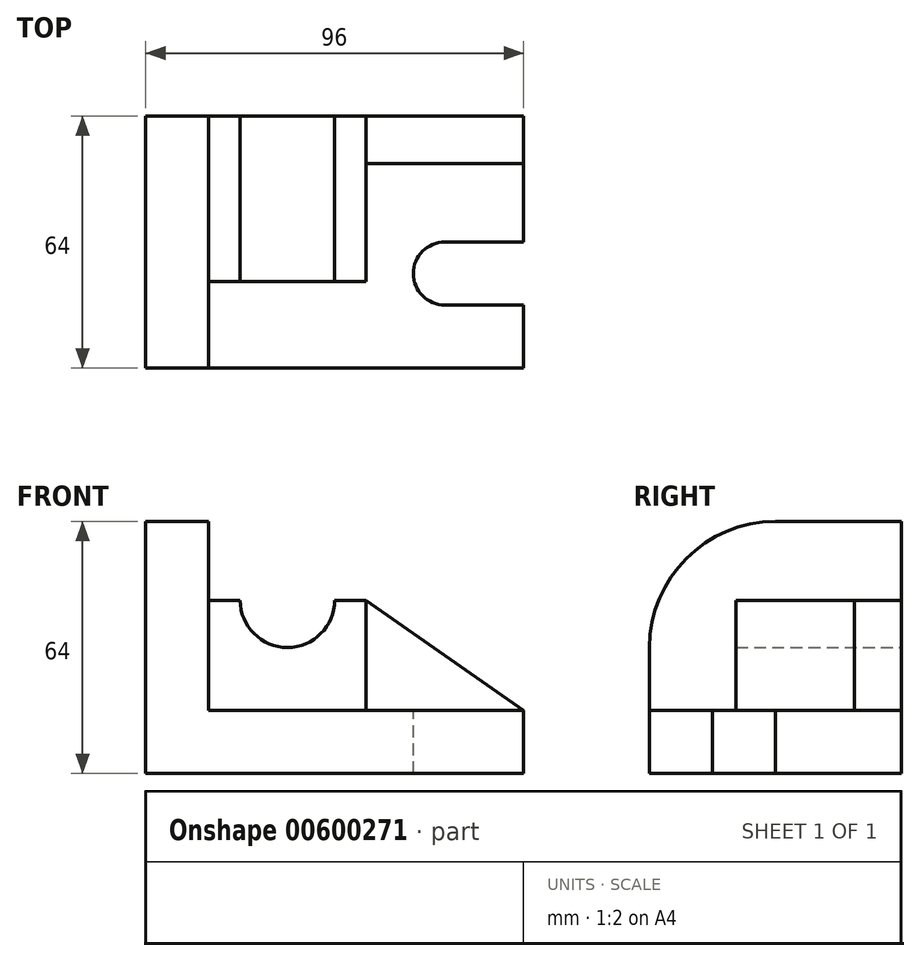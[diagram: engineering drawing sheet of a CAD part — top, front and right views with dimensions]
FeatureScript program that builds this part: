
annotation { "Feature Type Name" : "Feature", "Feature Type Description" : "" }
export const myFeature = defineFeature(function(context is Context, id is Id, definition is map)
    precondition{}
    {
        {
            var Q0;
            Q0=qCreatedBy(makeId("Top.planeOp"),FACE);
            var sketch = newSketch(context, id + "F0", { "sketchPlane" : qUnion([Q0])});
            skLineSegment(sketch, "E0.bottom", {"start": v(-48.61, -37.44) * mm, "end": v(47.39, -37.44) * mm});
            skLineSegment(sketch, "E0.top", {"start": v(-48.61, 26.56) * mm, "end": v(47.39, 26.56) * mm});
            skLineSegment(sketch, "E0.left", {"start": v(-48.61, -37.44) * mm, "end": v(-48.61, 26.56) * mm});
            skLineSegment(sketch, "E0.right", {"start": v(47.39, -37.44) * mm, "end": v(47.39, 26.56) * mm});
            skSolve(sketch);
        }
        {
            var Q0;
            Q0 = qSketchRegion(id + "F0", true);
            extrude(context, id + "F1", {"entities" : qUnion([Q0]), "depth" : 16 * mm, "offsetDistance" : 25 * mm});
        }
        {
            var Q0;
            Q0=makeQuery(id+"F1.opExtrude","SWEPT_FACE",FACE,{"disambiguationData":[OSD([sQuery(id+"F0.wireOp",EDGE,"E0.left")])]});
            var sketch = newSketch(context, id + "F2", { "sketchPlane" : qUnion([Q0])});
            skLineSegment(sketch, "E1", {"start": v(-26.56, 16) * mm, "end": v(-26.56, 64) * mm});
            skLineSegment(sketch, "E2", {"start": v(-26.56, 64) * mm, "end": v(5.44, 64) * mm});
            skLineSegment(sketch, "E3", {"start": v(-26.56, 16) * mm, "end": v(37.44, 16) * mm});
            skLineSegment(sketch, "E4", {"start": v(37.44, 16) * mm, "end": v(37.44, 32) * mm});
            skArc(sketch, "E5", {"start": v(5.44, 64) * mm, "mid": v(28.06, 54.63) * mm, "end": v(37.44, 32) * mm});
            skSolve(sketch);
        }
        {
            var Q0;
            Q0 = qSketchRegion(id + "F2", true);
            extrude(context, id + "F3", {"entities" : qUnion([Q0]), "operationType" : NewBodyOperationType.ADD, "oppositeDirection" : true, "depth" : 16 * mm, "offsetDistance" : 25 * mm});
        }
        {
            var Q0;
            Q0=makeQuery(id+"F3.boolean.opBoolean","MERGE",FACE,{"derivedFrom":[makeQuery(id+"F1.opExtrude","SWEPT_FACE",FACE,{"disambiguationData":[OSD([sQuery(id+"F0.wireOp",EDGE,"E0.top")])]}),makeQuery(id+"F3.opExtrude","SWEPT_FACE",FACE,{"disambiguationData":[OSD([sQuery(id+"F2.wireOp",EDGE,"E1")])]})]});
            var sketch = newSketch(context, id + "F4", { "sketchPlane" : qUnion([Q0])});
            skLineSegment(sketch, "E6", {"start": v(32.61, 16) * mm, "end": v(-7.39, 16) * mm});
            skLineSegment(sketch, "E7", {"start": v(-7.39, 16) * mm, "end": v(-7.39, 44) * mm});
            skLineSegment(sketch, "E8", {"start": v(-7.39, 44) * mm, "end": v(32.61, 44) * mm});
            skSolve(sketch);
        }
        {
            var Q0;
            {var subQ0=sQuery(id+"F4.wireOp",EDGE,"E6");Q0=makeQuery(id+"F4.imprint","IMPRINT",FACE,{"disambiguationData":[TD([[makeQuery(id+"F4.imprint","IMPRINT",EDGE,{"derivedFrom":subQ0}),-1.0]])]});}
            extrude(context, id + "F5", {"entities" : qUnion([Q0]), "operationType" : NewBodyOperationType.ADD, "oppositeDirection" : true, "depth" : 42 * mm, "offsetDistance" : 25 * mm});
        }
        {
            var Q0;
            {var subQ0=sQuery(id+"F2.wireOp",EDGE,"E1");Q0=makeQuery(id+"F5.boolean.opBoolean","MERGE",FACE,{"derivedFrom":[makeQuery(id+"F3.boolean.opBoolean","MERGE",FACE,{"derivedFrom":[makeQuery(id+"F1.opExtrude","SWEPT_FACE",FACE,{"disambiguationData":[OSD([sQuery(id+"F0.wireOp",EDGE,"E0.top")])]}),makeQuery(id+"F3.opExtrude","SWEPT_FACE",FACE,{"disambiguationData":[OSD([subQ0])]})]}),makeQuery(id+"F5.opExtrude","CAP_FACE",FACE,{"disambiguationData":[OSD([subQ0,sQuery(id+"F4.wireOp",EDGE,"E6"),sQuery(id+"F4.wireOp",EDGE,"E7"),sQuery(id+"F4.wireOp",EDGE,"E8")])],"isStart":true})]});}
            var sketch = newSketch(context, id + "F6", { "sketchPlane" : qUnion([Q0])});
            skArc(sketch, "E9", {"start": v(0.61, 44) * mm, "mid": v(12.61, 32) * mm, "end": v(24.61, 44) * mm});
            skLineSegment(sketch, "E10", {"start": v(0.61, 44) * mm, "end": v(24.61, 44) * mm});
            skSolve(sketch);
        }
        {
            var Q0;
            Q0 = qSketchRegion(id + "F6", true);
            extrude(context, id + "F7", {"entities" : qUnion([Q0]), "operationType" : NewBodyOperationType.REMOVE, "oppositeDirection" : true, "depth" : 42 * mm, "offsetDistance" : 25 * mm});
        }
        {
            var Q0;
            Q0=makeQuery(id+"F1.opExtrude","CAP_FACE",FACE,{"disambiguationData":[OSD([sQuery(id+"F0.wireOp",EDGE,"E0.bottom"),sQuery(id+"F0.wireOp",EDGE,"E0.top"),sQuery(id+"F0.wireOp",EDGE,"E0.left"),sQuery(id+"F0.wireOp",EDGE,"E0.right")])],"isStart":false});
            var sketch = newSketch(context, id + "F8", { "sketchPlane" : qUnion([Q0])});
            skLineSegment(sketch, "E11.bottom", {"start": v(47.39, -21.44) * mm, "end": v(27.39, -21.44) * mm});
            skLineSegment(sketch, "E11.top", {"start": v(47.39, -5.44) * mm, "end": v(27.39, -5.44) * mm});
            skLineSegment(sketch, "E11.left", {"start": v(47.39, -21.44) * mm, "end": v(47.39, -5.44) * mm});
            skLineSegment(sketch, "E11.right", {"start": v(27.39, -21.44) * mm, "end": v(27.39, -5.44) * mm});
            skArc(sketch, "E12", {"start": v(27.39, -21.44) * mm, "mid": v(19.39, -13.44) * mm, "end": v(27.39, -5.44) * mm});
            skSolve(sketch);
        }
        {
            var Q0;
            Q0=makeQuery(id+"F8.imprint","IMPRINT",FACE,{"disambiguationData":[TD([[makeQuery(id+"F8.imprint","IMPRINT",EDGE,{"derivedFrom":sQuery(id+"F8.wireOp",EDGE,"E11.right")}),1.0]])]});
            var Q1;
            Q1=makeQuery(id+"F8.imprint","IMPRINT",FACE,{"disambiguationData":[TD([[makeQuery(id+"F8.imprint","IMPRINT",EDGE,{"derivedFrom":sQuery(id+"F8.wireOp",EDGE,"E11.bottom")}),-1.0]])]});
            extrude(context, id + "F9", {"entities" : qUnion([Q0, Q1]), "operationType" : NewBodyOperationType.REMOVE, "oppositeDirection" : true, "depth" : 16 * mm, "offsetDistance" : 25 * mm});
        }
        {
            var Q0;
            {var subQ0=sQuery(id+"F2.wireOp",EDGE,"E1");Q0=makeQuery(id+"F5.boolean.opBoolean","MERGE",FACE,{"derivedFrom":[makeQuery(id+"F3.boolean.opBoolean","MERGE",FACE,{"derivedFrom":[makeQuery(id+"F1.opExtrude","SWEPT_FACE",FACE,{"disambiguationData":[OSD([sQuery(id+"F0.wireOp",EDGE,"E0.top")])]}),makeQuery(id+"F3.opExtrude","SWEPT_FACE",FACE,{"disambiguationData":[OSD([subQ0])]})]}),makeQuery(id+"F5.opExtrude","CAP_FACE",FACE,{"disambiguationData":[OSD([subQ0,sQuery(id+"F4.wireOp",EDGE,"E6"),sQuery(id+"F4.wireOp",EDGE,"E7"),sQuery(id+"F4.wireOp",EDGE,"E8")])],"isStart":true})]});}
            var sketch = newSketch(context, id + "F10", { "sketchPlane" : qUnion([Q0])});
            skLineSegment(sketch, "E13", {"start": v(-47.39, 16) * mm, "end": v(-7.39, 16) * mm});
            skLineSegment(sketch, "E14", {"start": v(-7.39, 16) * mm, "end": v(-7.39, 44) * mm});
            skLineSegment(sketch, "E15", {"start": v(-7.39, 44) * mm, "end": v(-47.39, 16) * mm});
            skSolve(sketch);
        }
        {
            var Q0;
            Q0 = qSketchRegion(id + "F10", true);
            extrude(context, id + "F11", {"entities" : qUnion([Q0]), "operationType" : NewBodyOperationType.ADD, "oppositeDirection" : true, "depth" : 12 * mm, "offsetDistance" : 25 * mm});
        }
    });
